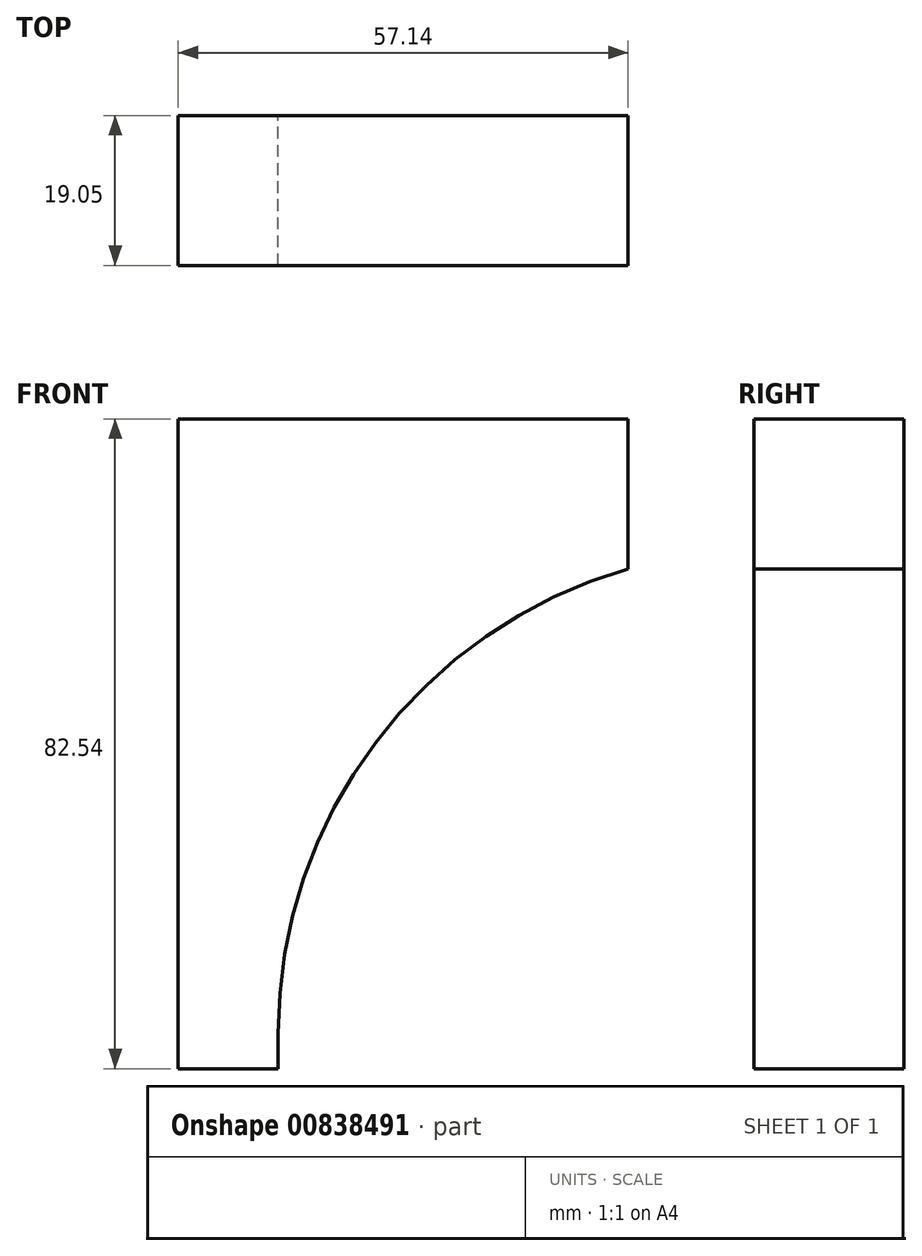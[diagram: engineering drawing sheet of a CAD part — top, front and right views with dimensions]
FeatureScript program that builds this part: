
annotation { "Feature Type Name" : "Feature", "Feature Type Description" : "" }
export const myFeature = defineFeature(function(context is Context, id is Id, definition is map)
    precondition{}
    {
        {
            var Q0;
            Q0=qCreatedBy(makeId("Front.planeOp"),FACE);
            var sketch = newSketch(context, id + "F0", { "sketchPlane" : qUnion([Q0])});
            skLineSegment(sketch, "E0.bottom", {"start": v(28.57, 41.28) * mm, "end": v(-28.58, 41.28) * mm});
            skLineSegment(sketch, "E0.top", {"start": v(-15.87, -41.28) * mm, "end": v(-28.57, -41.28) * mm});
            skLineSegment(sketch, "E0.left", {"start": v(28.57, 41.28) * mm, "end": v(28.57, 22.23) * mm});
            skLineSegment(sketch, "E0.right", {"start": v(-28.58, 41.28) * mm, "end": v(-28.57, -41.28) * mm});
            skPoint(sketch, "E0.middle", {"position": v(0, 0) * mm});
            skLineSegment(sketch, "E1", {"start": v(-15.87, -36.83) * mm, "end": v(-15.87, -41.28) * mm});
            skArc(sketch, "E2", {"start": v(-15.87, -36.83) * mm, "mid": v(-3.52, 0.13) * mm, "end": v(28.57, 22.23) * mm});
            skPoint(sketch, "E3.orphan", {"position": v(28.58, -41.28) * mm});
            skSolve(sketch);
        }
        {
            var Q0;
            Q0 = qSketchRegion(id + "F0", true);
            extrude(context, id + "F1", {"entities" : qUnion([Q0]), "depth" : 19.05 * mm, "offsetDistance" : 25.4 * mm});
        }
    });
